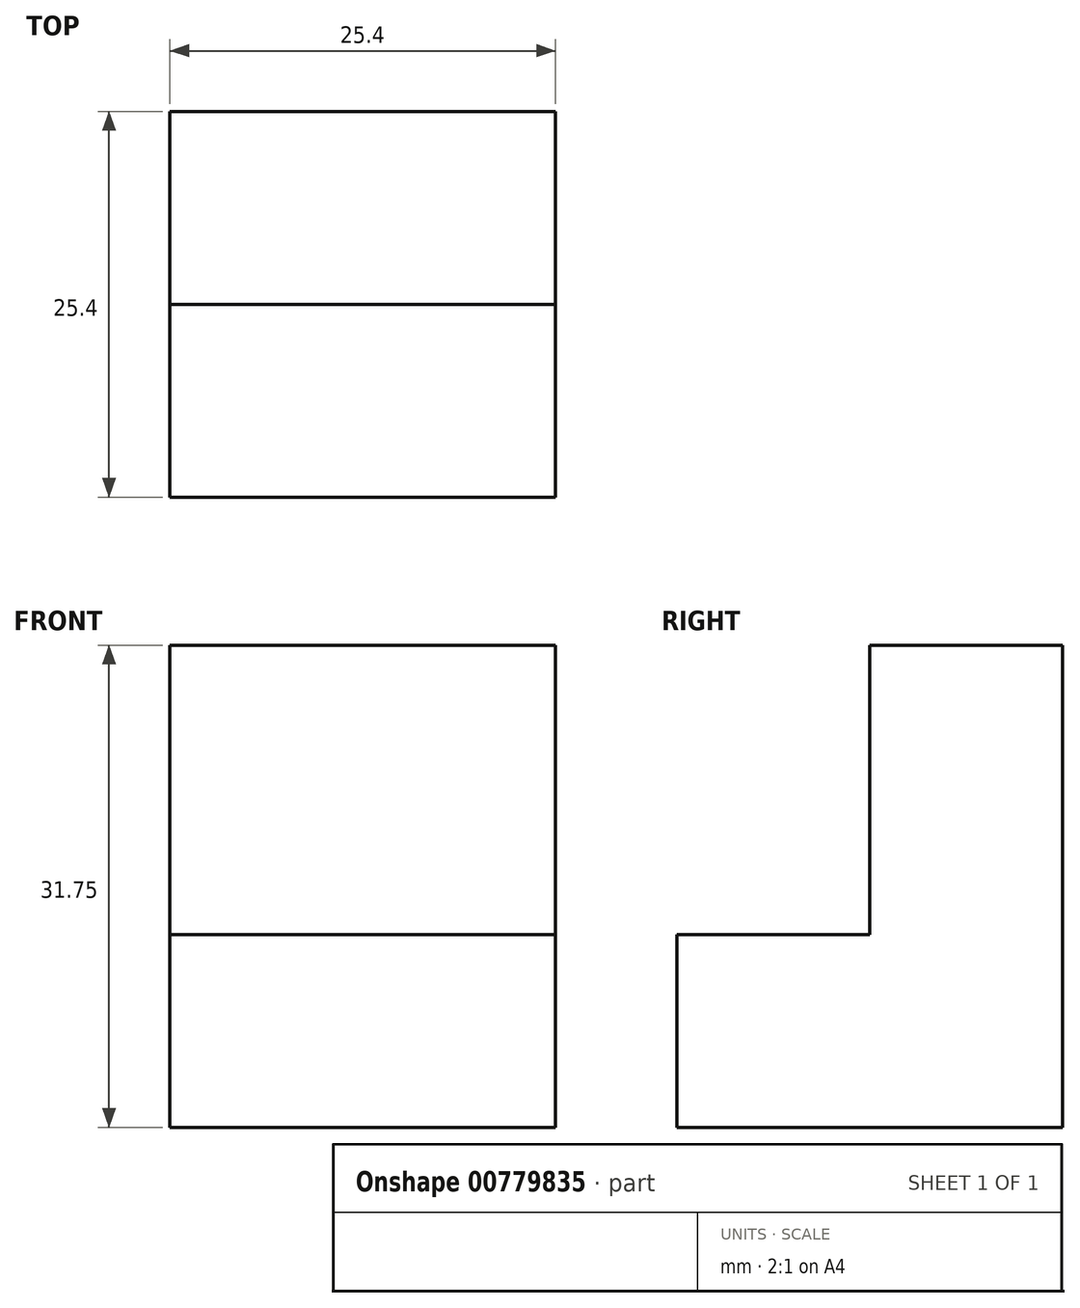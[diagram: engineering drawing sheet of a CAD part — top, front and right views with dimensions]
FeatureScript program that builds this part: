
annotation { "Feature Type Name" : "Feature", "Feature Type Description" : "" }
export const myFeature = defineFeature(function(context is Context, id is Id, definition is map)
    precondition{}
    {
        {
            var Q0;
            Q0=qCreatedBy(makeId("Right.planeOp"),FACE);
            var sketch = newSketch(context, id + "F0", { "sketchPlane" : qUnion([Q0])});
            skLineSegment(sketch, "E0", {"start": v(0, 0) * mm, "end": v(25.4, 0) * mm});
            skLineSegment(sketch, "E1", {"start": v(25.4, 0) * mm, "end": v(25.4, 31.75) * mm});
            skLineSegment(sketch, "E2", {"start": v(25.4, 31.75) * mm, "end": v(12.7, 31.75) * mm});
            skLineSegment(sketch, "E3", {"start": v(12.7, 31.75) * mm, "end": v(12.7, 12.7) * mm});
            skLineSegment(sketch, "E4", {"start": v(12.7, 12.7) * mm, "end": v(0, 12.7) * mm});
            skLineSegment(sketch, "E5", {"start": v(0, 12.7) * mm, "end": v(0, 0) * mm});
            skSolve(sketch);
        }
        {
            var Q0;
            Q0 = qSketchRegion(id + "F0", true);
            extrude(context, id + "F1", {"entities" : qUnion([Q0]), "depth" : 25.4 * mm, "offsetDistance" : 25.4 * mm});
        }
    });
